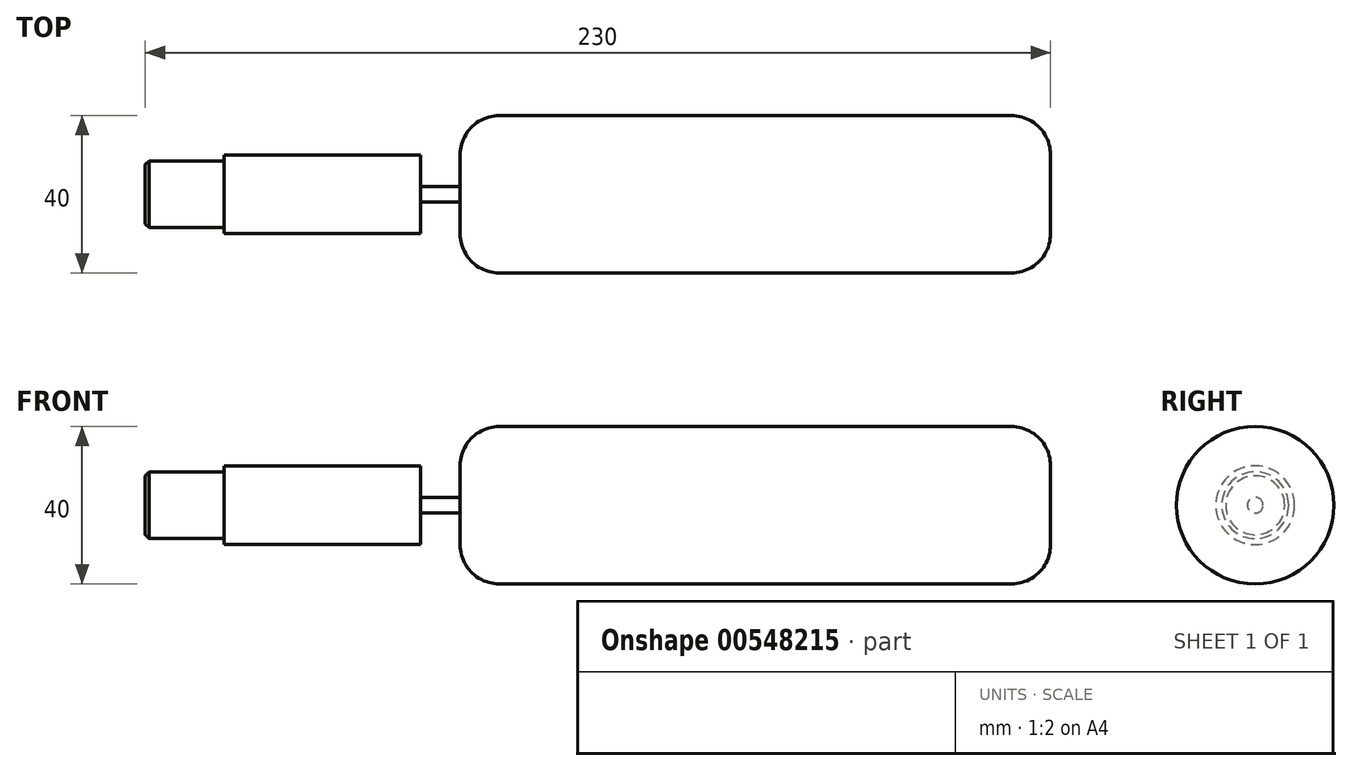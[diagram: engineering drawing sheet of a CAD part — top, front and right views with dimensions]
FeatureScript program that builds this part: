
annotation { "Feature Type Name" : "Feature", "Feature Type Description" : "" }
export const myFeature = defineFeature(function(context is Context, id is Id, definition is map)
    precondition{}
    {
        {
            var Q0;
            Q0=qCreatedBy(makeId("Top.planeOp"),FACE);
            var sketch = newSketch(context, id + "F0", { "sketchPlane" : qUnion([Q0])});
            skLineSegment(sketch, "E0.bottom", {"start": v(0, 0) * mm, "end": v(150, 0) * mm});
            skLineSegment(sketch, "E0.top", {"start": v(10, 20) * mm, "end": v(140, 20) * mm});
            skLineSegment(sketch, "E0.left", {"start": v(0, 0) * mm, "end": v(0, 10) * mm});
            skLineSegment(sketch, "E0.right", {"start": v(150, 0) * mm, "end": v(150, 10) * mm});
            skPoint(sketch, "E1.visualSharp", {"position": v(0, 20) * mm});
            skArc(sketch, "E1.filletArc", {"start": v(10, 20) * mm, "mid": v(2.93, 17.07) * mm, "end": v(0, 10) * mm});
            skPoint(sketch, "E2.visualSharp", {"position": v(150, 20) * mm});
            skArc(sketch, "E2.filletArc", {"start": v(150, 10) * mm, "mid": v(147.07, 17.07) * mm, "end": v(140, 20) * mm});
            skLineSegment(sketch, "E3.bottom", {"start": v(0, 0) * mm, "end": v(-10, 0) * mm});
            skLineSegment(sketch, "E3.top", {"start": v(0, 2) * mm, "end": v(-10, 2) * mm});
            skLineSegment(sketch, "E3.left", {"start": v(0, 0) * mm, "end": v(0, 2) * mm});
            skLineSegment(sketch, "E3.right", {"start": v(-10, 0) * mm, "end": v(-10, 2) * mm});
            skLineSegment(sketch, "E4.bottom", {"start": v(-10, 0) * mm, "end": v(-60, 0) * mm});
            skLineSegment(sketch, "E4.top", {"start": v(-10, 10) * mm, "end": v(-60, 10) * mm});
            skLineSegment(sketch, "E4.left", {"start": v(-10, 0) * mm, "end": v(-10, 10) * mm});
            skLineSegment(sketch, "E4.right", {"start": v(-60, 0) * mm, "end": v(-60, 10) * mm});
            skLineSegment(sketch, "E5.bottom", {"start": v(-60, 0) * mm, "end": v(-80, 0) * mm});
            skLineSegment(sketch, "E5.top", {"start": v(-60, 8.5) * mm, "end": v(-80, 8.5) * mm});
            skLineSegment(sketch, "E5.left", {"start": v(-60, 0) * mm, "end": v(-60, 8.5) * mm});
            skLineSegment(sketch, "E5.right", {"start": v(-80, 0) * mm, "end": v(-80, 8.5) * mm});
            skSolve(sketch);
        }
        {
            var Q0;
            Q0 = qSketchRegion(id + "F0", true);
            var Q1;
            Q1=sQuery(id+"F0.wireOp",EDGE,"E4.bottom");
            revolve(context, id + "F1", {"entities" : qUnion([Q0]), "axis" : qUnion([Q1]), "revolveType" : RevolveType.FULL});
        }
        {
            var Q0;
            Q0=makeQuery(id+"F1.opRevolve","SWEPT_EDGE",EDGE,{"disambiguationData":[OSD([sQuery(id+"F0.wireOp",EDGE,"E5.top"),sQuery(id+"F0.wireOp",EDGE,"E5.right")])]});
            chamfer(context, id + "F2", {"entities" : qUnion([Q0]), "width" : 1 * mm, "tangentPropagation" : true});
        }
    });
